# Revit family: РИДАН_Кран для теплосчетчика 187F
name_source: partatom
category: Арматура трубопроводов
units: mm (PartAtom-declared; Revit-internal decimal feet)

## family parameters
Всегда вертикально = Да
На основе рабочей плоскости = Нет
Общий = Нет
При загрузке вырезать с полостями = Нет
Размер круглого соединителя = Использовать диаметр
Тип детали = Вставляется

## types (3) — shared parameters
ADSK_Версия Revit = 2019
ADSK_Версия семейства = 1.0
ADSK_Единица измерения = шт.
ADSK_Завод-изготовитель = ООО «Ридан-Трейд»
ADSK_Количество = 1
ADSK_Потеря давления жидкости = 0.0 Па
ADSK_Расход жидкости = 0.0 м³/ч
LT = 187F
f = 35 мм
j = 16 мм

## per-type parameters (varying)
| type | ADSK_Диаметр условный | ADSK_Код изделия | ADSK_Марка | ADSK_Масса | ADSK_Наименование | ADSK_Пропускная способность | a | b | c | d | e | g | h | i | k | l | l1 | m |
| DN 15 | 15 мм | 187F0593R | 187F DN15 | 0.203 | Кран шаровой для подключения датчика температуры теплосчетчика PN16, Tmax=120C, DN15 | 15.0 м³/ч | 10 мм | 32 мм | 11 мм | 16 мм | 20 мм | 15 мм | 24 мм | 30 мм | 21 мм | 14 мм | 15 мм | 30 мм |
| DN 20 | 20 мм | 187F0592R | 187F DN20 | 0.311 | Кран шаровой для подключения датчика температуры теплосчетчика PN16, Tmax=120C, DN20 | 28.0 м³/ч | 10 мм | 37 мм | 10 мм | 19 мм | 22 мм | 21 мм | 31 мм | 37 мм | 26 мм | 17 мм | 17 мм | 35 мм |
| DN 25 | 25 мм | 187F0591R | 187F DN25 | 0.433 | Кран шаровой для подключения датчика температуры теплосчетчика PN16, Tmax=120C, DN25 | 39.0 м³/ч | 12 мм | 46 мм | 12 мм | 23 мм | 26 мм | 19 мм | 37 мм | 47 мм | 34 мм | 20 мм | 20 мм | 40 мм |
